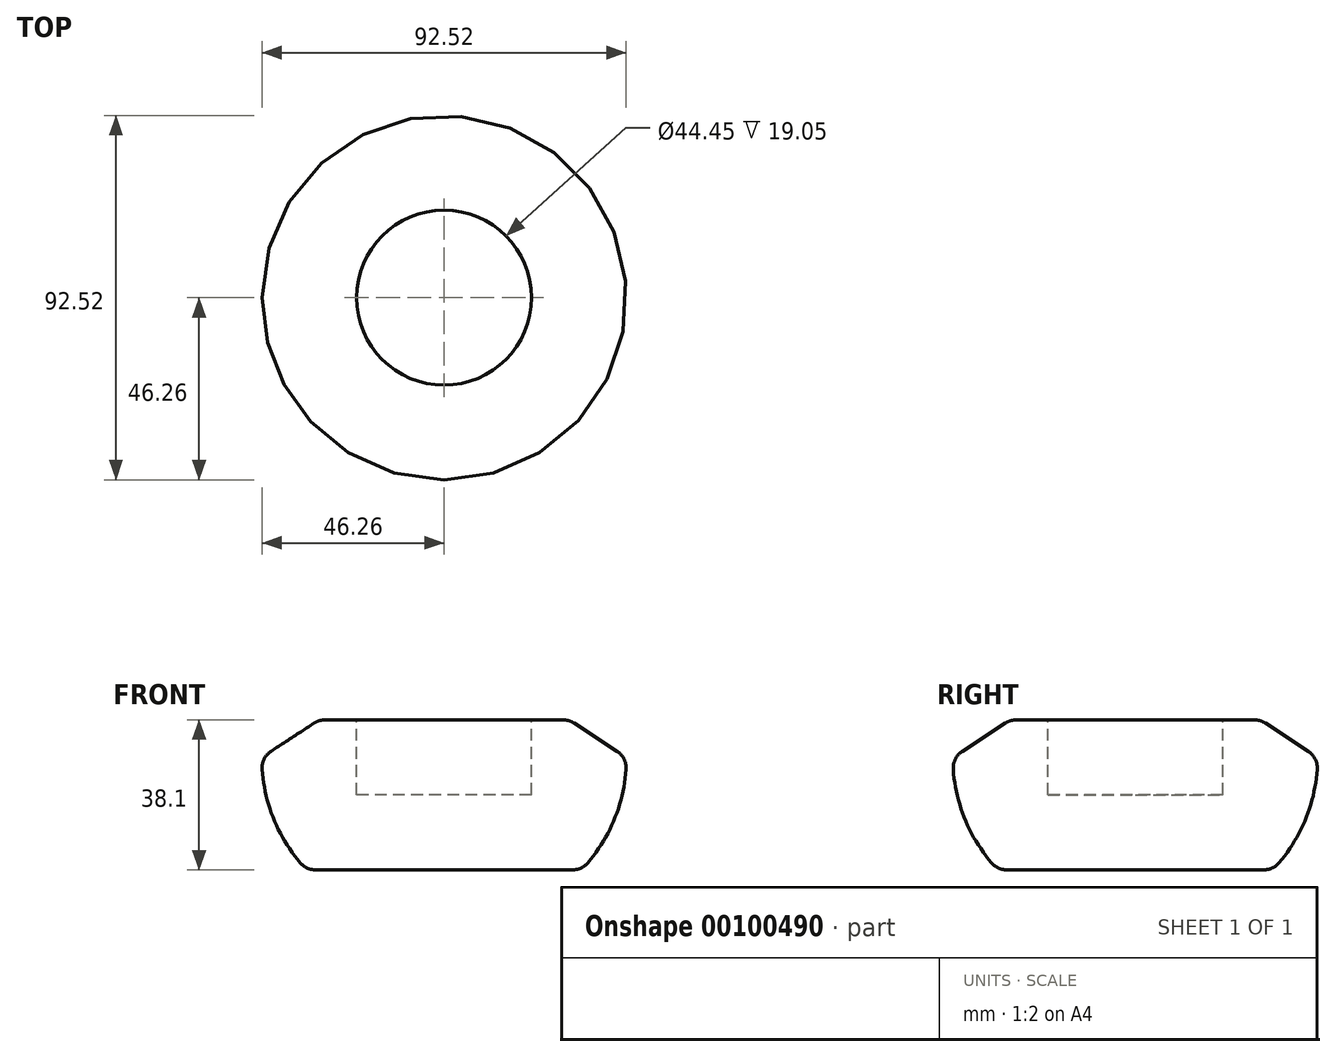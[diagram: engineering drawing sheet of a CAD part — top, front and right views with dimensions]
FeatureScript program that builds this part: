
annotation { "Feature Type Name" : "Feature", "Feature Type Description" : "" }
export const myFeature = defineFeature(function(context is Context, id is Id, definition is map)
    precondition{}
    {
        {
            var Q0;
            Q0=qCreatedBy(makeId("Front.planeOp"),FACE);
            var sketch = newSketch(context, id + "F0", { "sketchPlane" : qUnion([Q0])});
            skLineSegment(sketch, "E0", {"start": v(0, 55.4) * mm, "end": v(0, -36.25) * mm, "construction": true});
            skLineSegment(sketch, "E1", {"start": v(0, 0) * mm, "end": v(34.93, 0) * mm});
            skLineSegment(sketch, "E2", {"start": v(0, 38.1) * mm, "end": v(31.75, 38.1) * mm});
            skLineSegment(sketch, "E3", {"start": v(31.75, 38.1) * mm, "end": v(46.36, 28.58) * mm});
            skArc(sketch, "E4", {"start": v(34.93, 0) * mm, "mid": v(43.4, 13.19) * mm, "end": v(46.36, 28.58) * mm});
            skLineSegment(sketch, "E5", {"start": v(0, 38.1) * mm, "end": v(0, 0) * mm});
            skLineSegment(sketch, "E6", {"start": v(46.36, 28.58) * mm, "end": v(46.36, 51.2) * mm, "construction": true});
            skSolve(sketch);
        }
        {
            var Q0;
            Q0=makeQuery(id+"F0.imprint","IMPRINT",FACE,{"disambiguationData":[TD([[makeQuery(id+"F0.imprint","IMPRINT",EDGE,{"derivedFrom":sQuery(id+"F0.wireOp",EDGE,"E1")}),1.0]])]});
            var Q1;
            Q1=sQuery(id+"F0.wireOp",EDGE,"E0");
            revolve(context, id + "F1", {"entities" : qUnion([Q0]), "axis" : qUnion([Q1]), "revolveType" : RevolveType.FULL});
        }
        {
            var Q0;
            Q0=makeQuery(id+"F1.opRevolve","SWEPT_EDGE",EDGE,{"disambiguationData":[OSD([sQuery(id+"F0.wireOp",EDGE,"E3"),sQuery(id+"F0.wireOp",EDGE,"E4")])]});
            var Q1;
            Q1=makeQuery(id+"F1.opRevolve","SWEPT_EDGE",EDGE,{"disambiguationData":[OSD([sQuery(id+"F0.wireOp",EDGE,"E2"),sQuery(id+"F0.wireOp",EDGE,"E3")])]});
            var Q2;
            Q2=makeQuery(id+"F1.opRevolve","SWEPT_EDGE",EDGE,{"disambiguationData":[OSD([sQuery(id+"F0.wireOp",EDGE,"E1"),sQuery(id+"F0.wireOp",EDGE,"E4")])]});
            fillet(context, id + "F2", {"entities" : qUnion([Q0, Q1, Q2]), "radius" : 5.08 * mm, "tangentPropagation" : true, "allowEdgeOverflow" : false});
        }
        {
            var Q0;
            Q0=makeQuery(id+"F1.opRevolve","SWEPT_FACE",FACE,{"disambiguationData":[OSD([sQuery(id+"F0.wireOp",EDGE,"E2")])]});
            var sketch = newSketch(context, id + "F3", { "sketchPlane" : qUnion([Q0])});
            skCircle(sketch, "E7", {"center": v(0, 0) * mm, "radius": 22.23 * mm});
            skSolve(sketch);
        }
        {
            var Q0;
            Q0=makeQuery(id+"F3.imprint","IMPRINT",FACE,{"disambiguationData":[TD([[makeQuery(id+"F3.imprint","IMPRINT",EDGE,{"derivedFrom":sQuery(id+"F3.wireOp",EDGE,"E7")}),1.0]])]});
            extrude(context, id + "F4", {"entities" : qUnion([Q0]), "operationType" : NewBodyOperationType.REMOVE, "oppositeDirection" : true, "depth" : 19.05 * mm});
        }
    });
